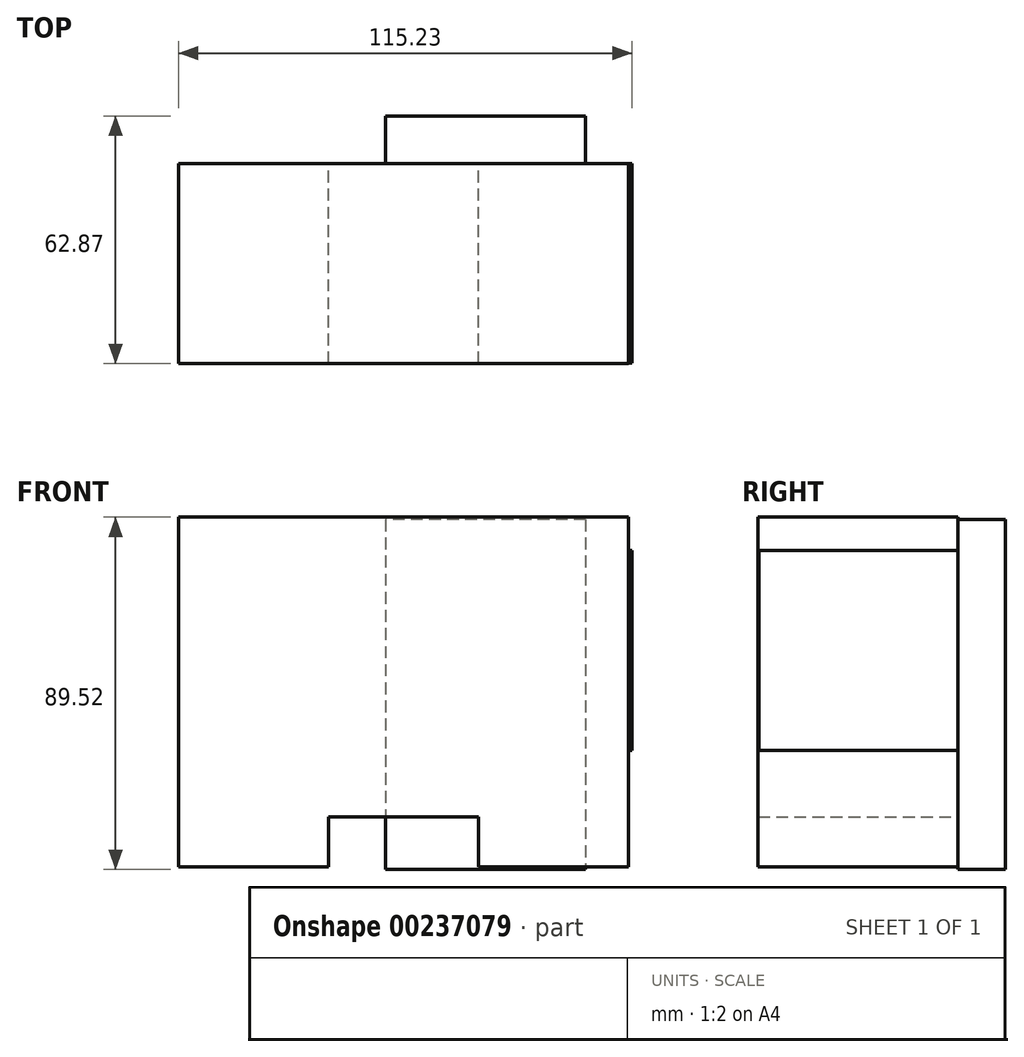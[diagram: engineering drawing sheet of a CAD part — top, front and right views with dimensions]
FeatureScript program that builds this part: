
annotation { "Feature Type Name" : "Feature", "Feature Type Description" : "" }
export const myFeature = defineFeature(function(context is Context, id is Id, definition is map)
    precondition{}
    {
        {
            var Q0;
            Q0=qCreatedBy(makeId("Front.planeOp"),FACE);
            var sketch = newSketch(context, id + "F0", { "sketchPlane" : qUnion([Q0])});
            skLineSegment(sketch, "E0", {"start": v(-52.62, 59.34) * mm, "end": v(61.68, 59.34) * mm});
            skLineSegment(sketch, "E1", {"start": v(-52.62, 59.34) * mm, "end": v(-52.62, -29.56) * mm});
            skLineSegment(sketch, "E2", {"start": v(-52.62, -29.56) * mm, "end": v(-14.52, -29.56) * mm});
            skLineSegment(sketch, "E3", {"start": v(-14.52, -29.56) * mm, "end": v(-14.52, -16.86) * mm});
            skLineSegment(sketch, "E4", {"start": v(-14.52, -16.86) * mm, "end": v(23.58, -16.86) * mm});
            skLineSegment(sketch, "E5", {"start": v(61.68, 59.34) * mm, "end": v(61.68, -29.56) * mm});
            skLineSegment(sketch, "E6", {"start": v(61.68, -29.56) * mm, "end": v(23.58, -29.56) * mm});
            skLineSegment(sketch, "E7", {"start": v(23.58, -16.86) * mm, "end": v(23.58, -29.56) * mm});
            skSolve(sketch);
        }
        {
            var Q0;
            Q0=makeQuery(id+"F0.imprint","IMPRINT",FACE,{"disambiguationData":[TD([[makeQuery(id+"F0.imprint","IMPRINT",EDGE,{"derivedFrom":sQuery(id+"F0.wireOp",EDGE,"E0")}),-1.0]])]});
            extrude(context, id + "F1", {"entities" : qUnion([Q0]), "depth" : 50.8 * mm});
        }
        {
            var Q0;
            Q0=qCreatedBy(makeId("Right.planeOp"),FACE);
            var sketch = newSketch(context, id + "F2", { "sketchPlane" : qUnion([Q0])});
            skLineSegment(sketch, "E8", {"start": v(12.07, 58.72) * mm, "end": v(12.07, -30.18) * mm});
            skLineSegment(sketch, "E9", {"start": v(12.07, 58.72) * mm, "end": v(0, 58.72) * mm});
            skLineSegment(sketch, "E10", {"start": v(0, 58.72) * mm, "end": v(0, -30.18) * mm});
            skLineSegment(sketch, "E11", {"start": v(0, -30.18) * mm, "end": v(12.07, -30.18) * mm});
            skSolve(sketch);
        }
        {
            var Q0;
            Q0=makeQuery(id+"F2.imprint","IMPRINT",FACE,{"disambiguationData":[TD([[makeQuery(id+"F2.imprint","IMPRINT",EDGE,{"derivedFrom":sQuery(id+"F2.wireOp",EDGE,"E8")}),-1.0]])]});
            extrude(context, id + "F3", {"entities" : qUnion([Q0]), "operationType" : NewBodyOperationType.ADD, "depth" : 50.8 * mm});
        }
        {
            var Q0;
            Q0=qCreatedBy(makeId("Top.planeOp"),FACE);
            var sketch = newSketch(context, id + "F4", { "sketchPlane" : qUnion([Q0])});
            skLineSegment(sketch, "E12", {"start": v(-51.69, 0) * mm, "end": v(62.61, 0) * mm});
            skLineSegment(sketch, "E13", {"start": v(-51.69, 0) * mm, "end": v(-51.69, -50.6) * mm});
            skLineSegment(sketch, "E14", {"start": v(-51.69, -50.6) * mm, "end": v(62.61, -50.6) * mm});
            skLineSegment(sketch, "E15", {"start": v(62.61, 0) * mm, "end": v(62.61, -50.6) * mm});
            skSolve(sketch);
        }
        {
            var Q0;
            Q0=makeQuery(id+"F4.imprint","IMPRINT",FACE,{"disambiguationData":[TD([[makeQuery(id+"F4.imprint","IMPRINT",EDGE,{"derivedFrom":sQuery(id+"F4.wireOp",EDGE,"E12")}),-1.0]])]});
            extrude(context, id + "F5", {"entities" : qUnion([Q0]), "operationType" : NewBodyOperationType.ADD, "depth" : 50.8 * mm});
        }
    });
